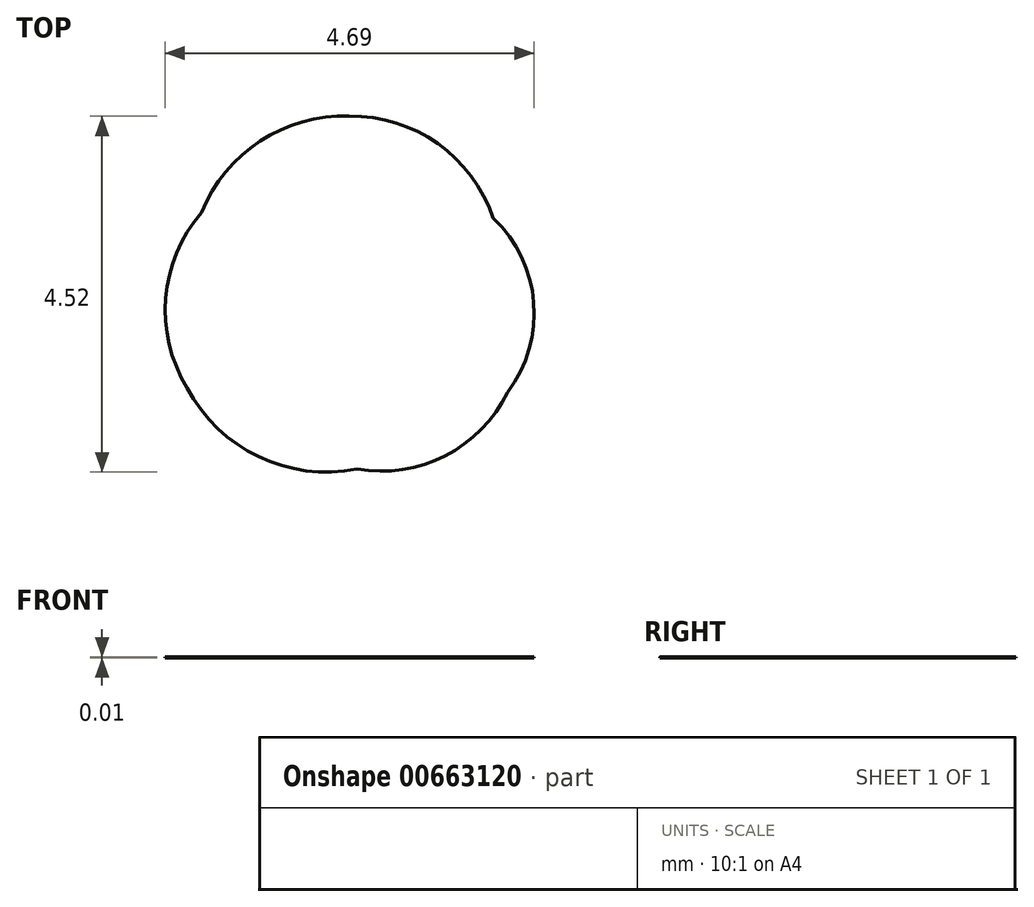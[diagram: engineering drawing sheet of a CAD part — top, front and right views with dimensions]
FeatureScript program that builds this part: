
annotation { "Feature Type Name" : "Feature", "Feature Type Description" : "" }
export const myFeature = defineFeature(function(context is Context, id is Id, definition is map)
    precondition{}
    {
        {
            var Q0;
            Q0=qCreatedBy(makeId("Top.planeOp"),FACE);
            var sketch = newSketch(context, id + "F0", { "sketchPlane" : qUnion([Q0])});
            skPoint(sketch, "E0.center", {"position": v(0, 0) * mm});
            skPoint(sketch, "E1.center", {"position": v(-0.03, 0.1) * mm});
            skLineSegment(sketch, "E2", {"start": v(7.76, 1.05) * mm, "end": v(7.76, 1.05) * mm});
            skLineSegment(sketch, "E3", {"start": v(8, -1.42) * mm, "end": v(8, -1.42) * mm});
            skLineSegment(sketch, "E4", {"start": v(6.33, 3.65) * mm, "end": v(6.36, 3.6) * mm});
            skArc(sketch, "E5", {"start": v(-0.1, 2.38) * mm, "mid": v(-1.23, 2.06) * mm, "end": v(-1.98, 1.16) * mm});
            skArc(sketch, "E6", {"start": v(-1.98, 1.16) * mm, "mid": v(-2.43, 0.07) * mm, "end": v(-2.16, -1.07) * mm});
            skArc(sketch, "E7", {"start": v(1.91, -1.13) * mm, "mid": v(2.24, 0.01) * mm, "end": v(1.73, 1.09) * mm});
            skArc(sketch, "E8", {"start": v(1.73, 1.09) * mm, "mid": v(1.03, 2.03) * mm, "end": v(-0.1, 2.38) * mm});
            skArc(sketch, "E9", {"start": v(-2.16, -1.07) * mm, "mid": v(-1.25, -1.95) * mm, "end": v(0, -2.1) * mm});
            skArc(sketch, "E10", {"start": v(0, -2.1) * mm, "mid": v(1.12, -1.93) * mm, "end": v(1.91, -1.13) * mm});
            skSolve(sketch);
        }
        {
            var Q0;
            Q0=makeQuery(id+"F0.imprint","IMPRINT",FACE,{"disambiguationData":[TD([[makeQuery(id+"F0.imprint","IMPRINT",EDGE,{"derivedFrom":sQuery(id+"F0.wireOp",EDGE,"E5")}),1.0]])]});
            extrude(context, id + "F1", {"entities" : qUnion([Q0]), "depth" : 5 / 406.4 * mm, "offsetDistance" : 25.4 * mm});
        }
    });
